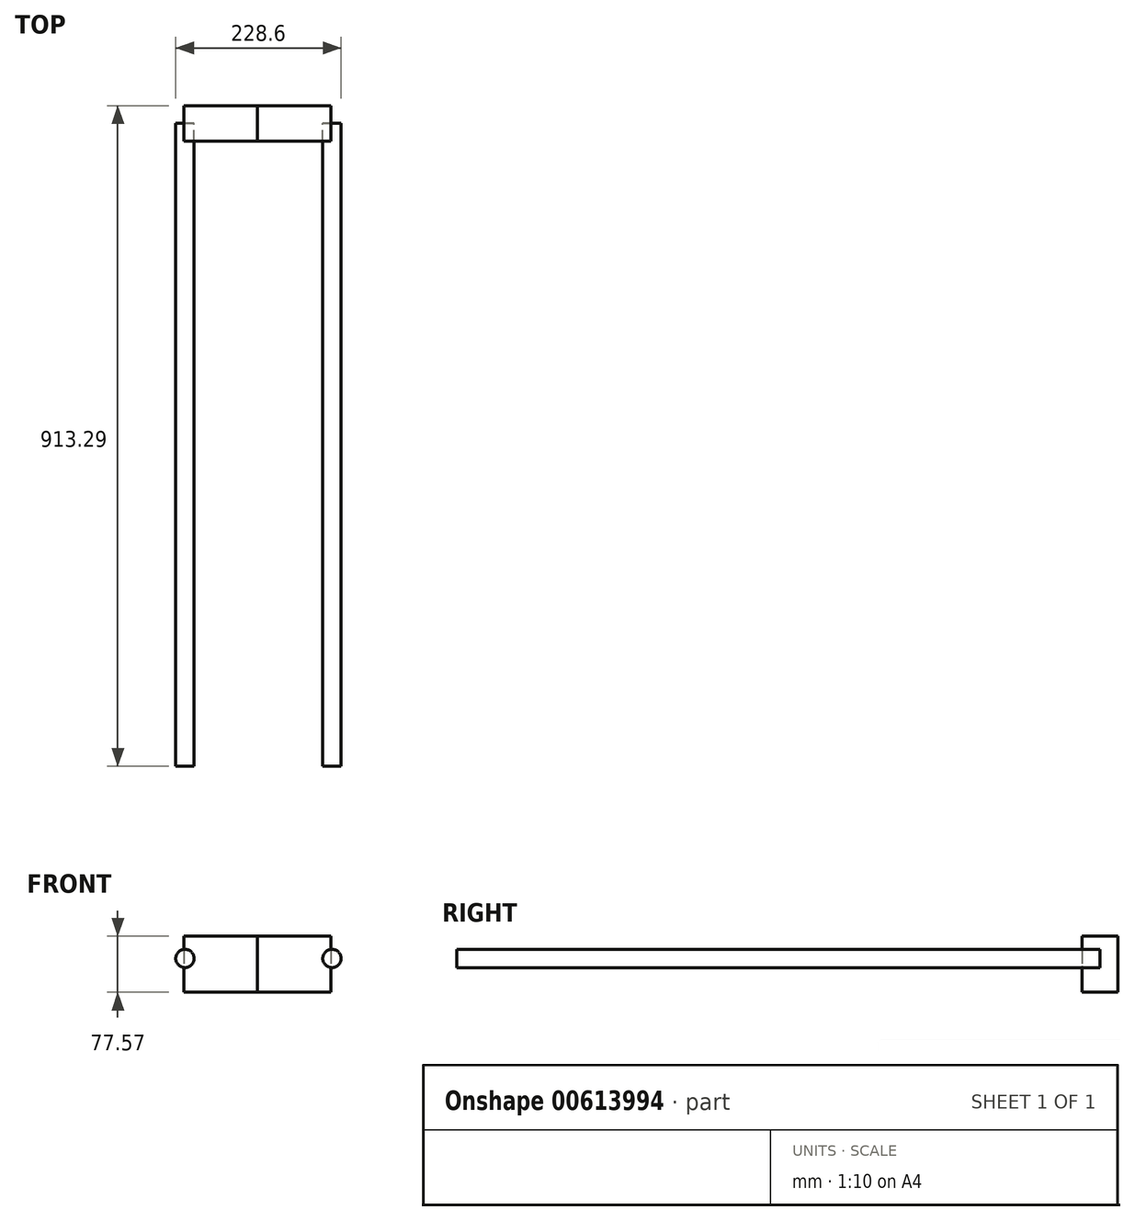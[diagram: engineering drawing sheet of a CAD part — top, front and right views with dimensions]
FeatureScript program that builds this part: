
annotation { "Feature Type Name" : "Feature", "Feature Type Description" : "" }
export const myFeature = defineFeature(function(context is Context, id is Id, definition is map)
    precondition{}
    {
        {
            var Q0;
            Q0=qCreatedBy(makeId("Front.planeOp"),FACE);
            var sketch = newSketch(context, id + "F0", { "sketchPlane" : qUnion([Q0])});
            skCircle(sketch, "E0", {"center": v(-100.04, 0) * mm, "radius": 12.7 * mm});
            skCircle(sketch, "E1", {"center": v(103.16, 0) * mm, "radius": 12.7 * mm});
            skSolve(sketch);
        }
        {
            var Q0;
            Q0=makeQuery(id+"F0.imprint","IMPRINT",FACE,{"disambiguationData":[TD([[makeQuery(id+"F0.imprint","IMPRINT",EDGE,{"derivedFrom":sQuery(id+"F0.wireOp",EDGE,"E0")}),1.0]])]});
            var Q1;
            Q1=makeQuery(id+"F0.imprint","IMPRINT",FACE,{"disambiguationData":[TD([[makeQuery(id+"F0.imprint","IMPRINT",EDGE,{"derivedFrom":sQuery(id+"F0.wireOp",EDGE,"E1")}),1.0]])]});
            extrude(context, id + "F1", {"entities" : qUnion([Q0, Q1]), "depth" : 889 * mm, "offsetDistance" : 25.4 * mm});
        }
        {
            var Q0;
            Q0=qCreatedBy(makeId("Right.planeOp"),FACE);
            var sketch = newSketch(context, id + "F2", { "sketchPlane" : qUnion([Q0])});
            skLineSegment(sketch, "E2.bottom", {"start": v(-24.68, 30.83) * mm, "end": v(24.29, 30.83) * mm});
            skLineSegment(sketch, "E2.top", {"start": v(-24.68, -46.74) * mm, "end": v(24.29, -46.74) * mm});
            skLineSegment(sketch, "E2.left", {"start": v(-24.68, 30.83) * mm, "end": v(-24.68, -46.74) * mm});
            skLineSegment(sketch, "E2.right", {"start": v(24.29, 30.83) * mm, "end": v(24.29, -46.74) * mm});
            skSolve(sketch);
        }
        {
            var Q0;
            Q0=makeQuery(id+"F2.imprint","IMPRINT",FACE,{"disambiguationData":[TD([[makeQuery(id+"F2.imprint","IMPRINT",EDGE,{"derivedFrom":sQuery(id+"F2.wireOp",EDGE,"E2.bottom")}),-1.0]])]});
            extrude(context, id + "F3", {"entities" : qUnion([Q0]), "oppositeDirection" : true, "depth" : 101.6 * mm, "offsetDistance" : 25.4 * mm});
        }
        {
            var Q0;
            Q0=makeQuery(id+"F3.opExtrude","CAP_FACE",FACE,{"disambiguationData":[OSD([sQuery(id+"F2.wireOp",EDGE,"E2.bottom"),sQuery(id+"F2.wireOp",EDGE,"E2.top"),sQuery(id+"F2.wireOp",EDGE,"E2.left"),sQuery(id+"F2.wireOp",EDGE,"E2.right")])],"isStart":false});
            var sketch = newSketch(context, id + "F4", { "sketchPlane" : qUnion([Q0])});
            skArc(sketch, "E3", {"start": v(888.09, 12.6) * mm, "mid": v(444.04, 250.48) * mm, "end": v(0, 12.6) * mm});
            skLineSegment(sketch, "E4", {"start": v(116.45, 138.02) * mm, "end": v(116.45, 13.04) * mm});
            skLineSegment(sketch, "E5", {"start": v(223.37, 202.69) * mm, "end": v(223.37, 13.2) * mm});
            skLineSegment(sketch, "E6", {"start": v(320.67, 236.02) * mm, "end": v(320.67, 12.7) * mm});
            skLineSegment(sketch, "E7", {"start": v(428.37, 250.25) * mm, "end": v(428.37, 13.88) * mm});
            skLineSegment(sketch, "E8", {"start": v(428.37, 13.88) * mm, "end": v(551.07, 239.63) * mm});
            skLineSegment(sketch, "E9", {"start": v(551.07, 239.63) * mm, "end": v(551.07, 13.82) * mm});
            skLineSegment(sketch, "E10", {"start": v(551.07, 13.82) * mm, "end": v(694.63, 187.95) * mm});
            skLineSegment(sketch, "E11", {"start": v(694.63, 14.6) * mm, "end": v(694.63, 187.95) * mm});
            skLineSegment(sketch, "E12", {"start": v(116.45, 13.04) * mm, "end": v(223.37, 202.69) * mm});
            skLineSegment(sketch, "E13", {"start": v(223.37, 202.69) * mm, "end": v(320.67, 12.7) * mm});
            skLineSegment(sketch, "E14", {"start": v(320.67, 236.02) * mm, "end": v(428.37, 13.88) * mm});
            skLineSegment(sketch, "E15", {"start": v(799.32, 114.94) * mm, "end": v(799.32, 12.7) * mm});
            skLineSegment(sketch, "E16", {"start": v(799.32, 12.7) * mm, "end": v(694.63, 187.95) * mm});
            skSolve(sketch);
        }
        {
            var Q0;
            Q0=makeQuery(id+"F3.opExtrude","CAP_FACE",FACE,{"disambiguationData":[OSD([sQuery(id+"F2.wireOp",EDGE,"E2.bottom"),sQuery(id+"F2.wireOp",EDGE,"E2.top"),sQuery(id+"F2.wireOp",EDGE,"E2.left"),sQuery(id+"F2.wireOp",EDGE,"E2.right")])],"isStart":true});
            extrude(context, id + "F5", {"entities" : qUnion([Q0]), "depth" : 101.6 * mm, "offsetDistance" : 25.4 * mm});
        }
        {
            var Q0;
            Q0=makeQuery(id+"F5.opExtrude","CAP_FACE",FACE,{"disambiguationData":[OSD([sQuery(id+"F2.wireOp",EDGE,"E2.bottom"),sQuery(id+"F2.wireOp",EDGE,"E2.top"),sQuery(id+"F2.wireOp",EDGE,"E2.left"),sQuery(id+"F2.wireOp",EDGE,"E2.right")])],"isStart":false});
            var sketch = newSketch(context, id + "F6", { "sketchPlane" : qUnion([Q0])});
            skArc(sketch, "E17", {"start": v(0, 12.92) * mm, "mid": v(-444.58, 249.8) * mm, "end": v(-889, 12.62) * mm});
            skLineSegment(sketch, "E18", {"start": v(-114.85, 136.34) * mm, "end": v(-114.85, 15.13) * mm});
            skLineSegment(sketch, "E19", {"start": v(-114.85, 15.13) * mm, "end": v(-223.38, 202.05) * mm});
            skLineSegment(sketch, "E20", {"start": v(-223.38, 202.05) * mm, "end": v(-223.38, 13) * mm});
            skLineSegment(sketch, "E21", {"start": v(-319.69, 235.08) * mm, "end": v(-319.69, 13) * mm});
            skLineSegment(sketch, "E22", {"start": v(-427.86, 249.55) * mm, "end": v(-427.86, 14.07) * mm});
            skLineSegment(sketch, "E23", {"start": v(-427.86, 14.07) * mm, "end": v(-551.96, 238.89) * mm});
            skLineSegment(sketch, "E24", {"start": v(-551.96, 238.89) * mm, "end": v(-551.96, 14.07) * mm});
            skLineSegment(sketch, "E25", {"start": v(-551.96, 14.07) * mm, "end": v(-694.2, 187.94) * mm});
            skLineSegment(sketch, "E26", {"start": v(-694.2, 187.94) * mm, "end": v(-694.2, 14.07) * mm});
            skLineSegment(sketch, "E27", {"start": v(-800.44, 114.23) * mm, "end": v(-800.44, 14.07) * mm});
            skLineSegment(sketch, "E28", {"start": v(-223.38, 202.05) * mm, "end": v(-319.69, 13) * mm});
            skLineSegment(sketch, "E29", {"start": v(-319.69, 235.08) * mm, "end": v(-427.86, 14.07) * mm});
            skLineSegment(sketch, "E30", {"start": v(-694.2, 187.94) * mm, "end": v(-800.44, 14.07) * mm});
            skSolve(sketch);
        }
        {
            var Q0;
            Q0=sQuery(id+"F6.wireOp",VERTEX,"E22.start");
            var Q1;
            Q1=sQuery(id+"F4.wireOp",VERTEX,"E7.start");
            var Q2;
            Q2=sQuery(id+"F4.wireOp",VERTEX,"E6.start");
            cPlane(context, id + "F7", {"entities" : qUnion([Q0, Q1, Q2]), "cplaneType" : CPlaneType.THREE_POINT, "offset" : 25.4 * mm, "width" : 152.4 * mm, "height" : 152.4 * mm});
        }
        {
            var Q0;
            Q0=qCreatedBy(id+"F7.planeOp",FACE);
            var sketch = newSketch(context, id + "F8", { "sketchPlane" : qUnion([Q0])});
            skLineSegment(sketch, "E31", {"start": v(100.36, -456.82) * mm, "end": v(-103.43, -456.82) * mm});
            skLineSegment(sketch, "E32", {"start": v(-103.43, -456.82) * mm, "end": v(-103.43, -346.71) * mm});
            skLineSegment(sketch, "E33", {"start": v(-103.43, -346.71) * mm, "end": v(101.24, -346.71) * mm});
            skLineSegment(sketch, "E34", {"start": v(101.24, -346.71) * mm, "end": v(100.36, -456.82) * mm});
            skLineSegment(sketch, "E35", {"start": v(-103.43, -456.82) * mm, "end": v(101.24, -346.71) * mm});
            skLineSegment(sketch, "E36", {"start": v(100.36, -456.82) * mm, "end": v(-103.43, -346.71) * mm});
            skSolve(sketch);
        }
        {
            var Q0;
            Q0=sQuery(id+"F4.wireOp",VERTEX,"E7.start");
            var Q1;
            Q1=sQuery(id+"F6.wireOp",VERTEX,"E22.start");
            var Q2;
            Q2=sQuery(id+"F6.wireOp",VERTEX,"E24.start");
            cPlane(context, id + "F9", {"entities" : qUnion([Q0, Q1, Q2]), "cplaneType" : CPlaneType.THREE_POINT, "offset" : 25.4 * mm, "width" : 152.4 * mm, "height" : 152.4 * mm});
        }
        {
            var Q0;
            Q0=qCreatedBy(id+"F9.planeOp",FACE);
            var sketch = newSketch(context, id + "F10", { "sketchPlane" : qUnion([Q0])});
            skLineSegment(sketch, "E37", {"start": v(-101.58, -404.87) * mm, "end": v(-101.58, -527.8) * mm});
            skLineSegment(sketch, "E38", {"start": v(-101.58, -527.8) * mm, "end": v(99.34, -527.8) * mm});
            skLineSegment(sketch, "E39", {"start": v(99.34, -527.8) * mm, "end": v(99.34, -401.48) * mm});
            skLineSegment(sketch, "E40", {"start": v(99.34, -401.48) * mm, "end": v(-101.58, -404.87) * mm});
            skLineSegment(sketch, "E41", {"start": v(99.34, -527.8) * mm, "end": v(-101.58, -404.87) * mm});
            skLineSegment(sketch, "E42", {"start": v(99.34, -401.48) * mm, "end": v(-101.58, -527.8) * mm});
            skSolve(sketch);
        }
        {
            var Q0;
            Q0=sQuery(id+"F10.wireOp",VERTEX,"E38.start");
            var Q1;
            Q1=sQuery(id+"F10.wireOp",VERTEX,"E41.start");
            var Q2;
            Q2=sQuery(id+"F6.wireOp",VERTEX,"E26.start");
            cPlane(context, id + "F11", {"entities" : qUnion([Q0, Q1, Q2]), "cplaneType" : CPlaneType.THREE_POINT, "offset" : 25.4 * mm, "width" : 152.4 * mm, "height" : 152.4 * mm});
        }
        {
            var Q0;
            Q0=qCreatedBy(id+"F11.planeOp",FACE);
            var sketch = newSketch(context, id + "F12", { "sketchPlane" : qUnion([Q0])});
            skLineSegment(sketch, "E43", {"start": v(-102.97, -438.39) * mm, "end": v(100.47, -438.39) * mm});
            skLineSegment(sketch, "E44", {"start": v(100.47, -438.39) * mm, "end": v(100.47, -591.16) * mm});
            skLineSegment(sketch, "E45", {"start": v(100.47, -591.16) * mm, "end": v(-101.87, -591.16) * mm});
            skLineSegment(sketch, "E46", {"start": v(-101.87, -591.16) * mm, "end": v(-102.97, -438.39) * mm});
            skLineSegment(sketch, "E47", {"start": v(-102.97, -438.39) * mm, "end": v(100.47, -591.16) * mm});
            skLineSegment(sketch, "E48", {"start": v(100.47, -438.39) * mm, "end": v(-101.87, -591.16) * mm});
            skSolve(sketch);
        }
        {
            var Q0;
            Q0=sQuery(id+"F12.wireOp",VERTEX,"E48.end");
            var Q1;
            Q1=sQuery(id+"F12.wireOp",VERTEX,"E44.end");
            var Q2;
            Q2=sQuery(id+"F6.wireOp",VERTEX,"E27.start");
            cPlane(context, id + "F13", {"entities" : qUnion([Q0, Q1, Q2]), "cplaneType" : CPlaneType.THREE_POINT, "offset" : 25.4 * mm, "width" : 152.4 * mm, "height" : 152.4 * mm});
        }
        {
            var Q0;
            Q0=sQuery(id+"F6.wireOp",VERTEX,"E21.start");
            var Q1;
            Q1=sQuery(id+"F8.wireOp",VERTEX,"E36.end");
            var Q2;
            Q2=sQuery(id+"F4.wireOp",VERTEX,"E5.start");
            cPlane(context, id + "F14", {"entities" : qUnion([Q0, Q1, Q2]), "cplaneType" : CPlaneType.THREE_POINT, "offset" : 25.4 * mm, "width" : 152.4 * mm, "height" : 152.4 * mm});
        }
        {
            var Q0;
            Q0=qCreatedBy(id+"F14.planeOp",FACE);
            var sketch = newSketch(context, id + "F15", { "sketchPlane" : qUnion([Q0])});
            skLineSegment(sketch, "E49", {"start": v(-104.07, -378.88) * mm, "end": v(-104.07, -277.76) * mm});
            skLineSegment(sketch, "E50", {"start": v(-104.07, -277.76) * mm, "end": v(100.76, -277.76) * mm});
            skLineSegment(sketch, "E51", {"start": v(100.76, -277.76) * mm, "end": v(100.76, -378.4) * mm});
            skLineSegment(sketch, "E52", {"start": v(100.76, -378.4) * mm, "end": v(-104.07, -378.88) * mm});
            skLineSegment(sketch, "E53", {"start": v(100.76, -277.76) * mm, "end": v(-104.07, -378.88) * mm});
            skLineSegment(sketch, "E54", {"start": v(100.76, -378.4) * mm, "end": v(-104.07, -277.76) * mm});
            skSolve(sketch);
        }
        {
            var Q0;
            Q0=sQuery(id+"F15.wireOp",VERTEX,"E51.start");
            var Q1;
            Q1=sQuery(id+"F15.wireOp",VERTEX,"E50.start");
            var Q2;
            Q2=sQuery(id+"F4.wireOp",VERTEX,"E4.start");
            cPlane(context, id + "F16", {"entities" : qUnion([Q0, Q1, Q2]), "cplaneType" : CPlaneType.THREE_POINT, "offset" : 25.4 * mm, "width" : 152.4 * mm, "height" : 152.4 * mm});
        }
    });
